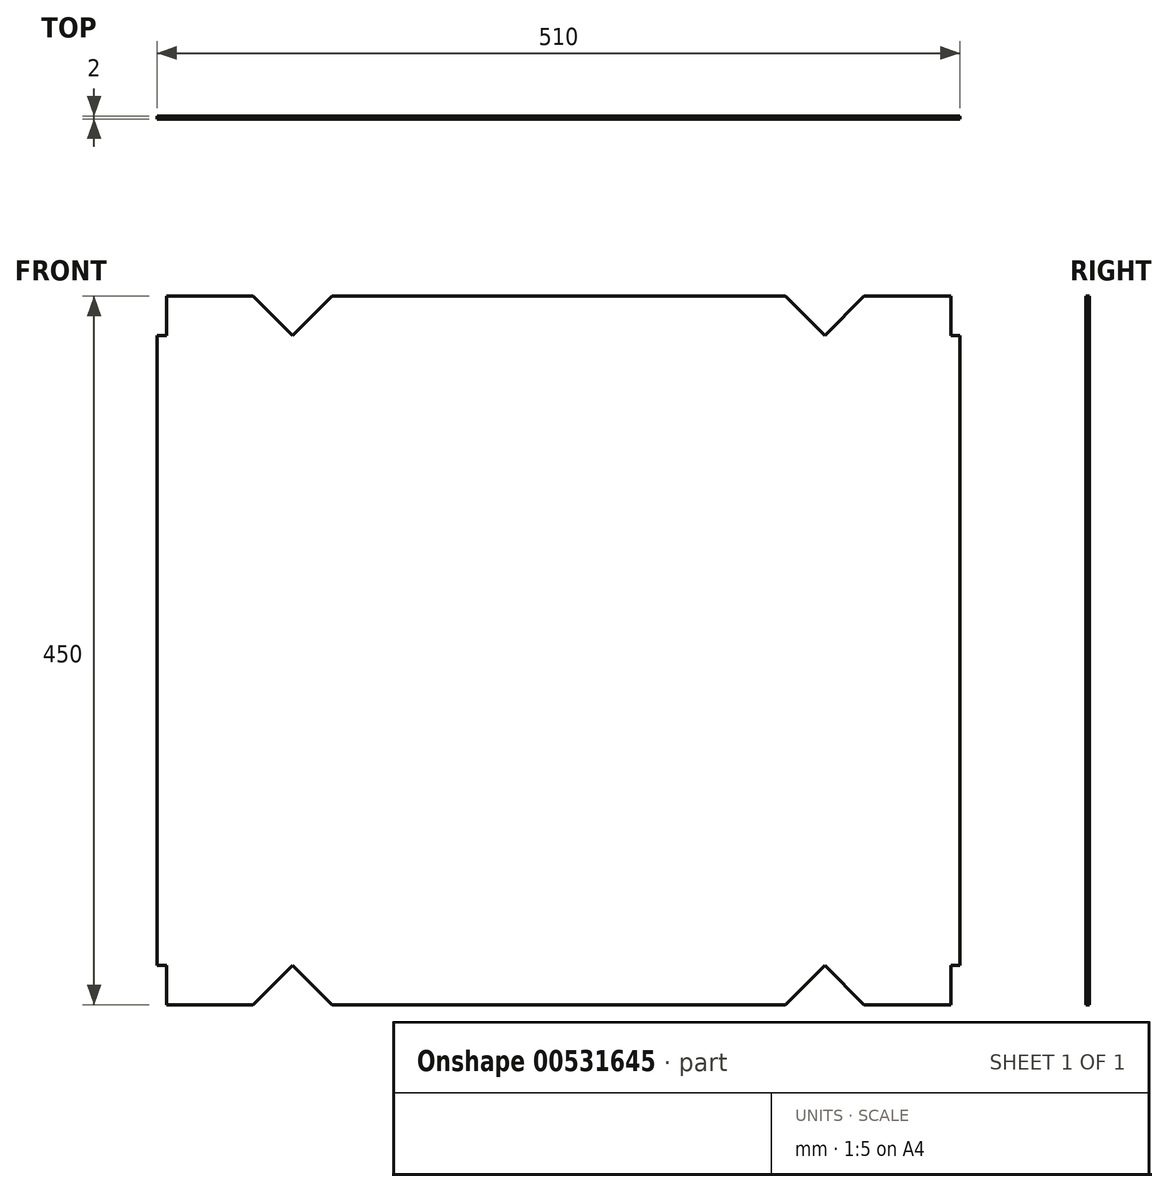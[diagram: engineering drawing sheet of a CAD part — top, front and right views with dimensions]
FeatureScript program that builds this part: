
annotation { "Feature Type Name" : "Feature", "Feature Type Description" : "" }
export const myFeature = defineFeature(function(context is Context, id is Id, definition is map)
    precondition{}
    {
        {
            var Q0;
            Q0=qCreatedBy(makeId("Front.planeOp"),FACE);
            var sketch = newSketch(context, id + "F0", { "sketchPlane" : qUnion([Q0])});
            skLineSegment(sketch, "E0.bottom", {"start": v(-246.48, 251.43) * mm, "end": v(-191.48, 251.43) * mm});
            skLineSegment(sketch, "E0.top", {"start": v(-246.48, -198.57) * mm, "end": v(-191.48, -198.57) * mm});
            skLineSegment(sketch, "E0.left", {"start": v(-252.48, 226.43) * mm, "end": v(-252.48, -173.57) * mm});
            skLineSegment(sketch, "E0.right", {"start": v(257.52, 226.43) * mm, "end": v(257.52, -173.57) * mm});
            skLineSegment(sketch, "E1.top", {"start": v(-252.48, 226.43) * mm, "end": v(-246.48, 226.43) * mm});
            skLineSegment(sketch, "E1.right", {"start": v(-246.48, 251.43) * mm, "end": v(-246.48, 226.43) * mm});
            skLineSegment(sketch, "E2.MirrorCS", {"start": v(251.52, 251.43) * mm, "end": v(251.52, 226.43) * mm});
            skLineSegment(sketch, "E3.MirrorCS", {"start": v(257.52, 226.43) * mm, "end": v(251.52, 226.43) * mm});
            skPoint(sketch, "E4.orphan", {"position": v(257.52, 251.43) * mm});
            skPoint(sketch, "E5.orphan", {"position": v(-252.48, 251.43) * mm});
            skLineSegment(sketch, "E6", {"start": v(-166.48, 226.43) * mm, "end": v(-141.48, 251.43) * mm});
            skLineSegment(sketch, "E7", {"start": v(-141.48, 251.43) * mm, "end": v(-166.48, 226.43) * mm});
            skLineSegment(sketch, "E8", {"start": v(-166.48, 226.43) * mm, "end": v(-191.48, 251.43) * mm});
            skLineSegment(sketch, "E9", {"start": v(-191.48, 251.43) * mm, "end": v(-166.48, 226.43) * mm});
            skLineSegment(sketch, "E10.MirrorCS", {"start": v(196.52, 251.43) * mm, "end": v(171.52, 226.43) * mm});
            skLineSegment(sketch, "E11.MirrorCS", {"start": v(171.52, 226.43) * mm, "end": v(146.52, 251.43) * mm});
            skLineSegment(sketch, "E12.trimOffspring", {"start": v(-141.48, 251.43) * mm, "end": v(146.52, 251.43) * mm});
            skLineSegment(sketch, "E13.trimOffspring", {"start": v(196.52, 251.43) * mm, "end": v(251.52, 251.43) * mm});
            skLineSegment(sketch, "E14", {"start": v(257.52, 226.43) * mm, "end": v(257.52, 26.43) * mm});
            skLineSegment(sketch, "E15.MirrorCS", {"start": v(171.52, -173.57) * mm, "end": v(146.52, -198.57) * mm});
            skLineSegment(sketch, "E16.MirrorCS", {"start": v(196.52, -198.57) * mm, "end": v(171.52, -173.57) * mm});
            skLineSegment(sketch, "E17.MirrorCS", {"start": v(251.52, -198.57) * mm, "end": v(251.52, -173.57) * mm});
            skLineSegment(sketch, "E18.MirrorCS", {"start": v(257.52, -173.57) * mm, "end": v(251.52, -173.57) * mm});
            skPoint(sketch, "E19.endSnap0", {"position": v(-252.48, 13.93) * mm});
            skLineSegment(sketch, "E20.MirrorCS", {"start": v(-191.48, -198.57) * mm, "end": v(-166.48, -173.57) * mm});
            skLineSegment(sketch, "E21.MirrorCS", {"start": v(-141.48, -198.57) * mm, "end": v(-166.48, -173.57) * mm});
            skLineSegment(sketch, "E22.MirrorCS", {"start": v(-246.48, -198.57) * mm, "end": v(-246.48, -173.57) * mm});
            skLineSegment(sketch, "E23.MirrorCS", {"start": v(-252.48, -173.57) * mm, "end": v(-246.48, -173.57) * mm});
            skPoint(sketch, "E19.end.orphan", {"position": v(-252.48, 26.43) * mm});
            skPoint(sketch, "E24.orphan", {"position": v(-252.48, -198.57) * mm});
            skLineSegment(sketch, "E25.trimOffspring", {"start": v(-141.48, -198.57) * mm, "end": v(146.52, -198.57) * mm});
            skLineSegment(sketch, "E26.trimOffspring", {"start": v(196.52, -198.57) * mm, "end": v(251.52, -198.57) * mm});
            skPoint(sketch, "E27.end.orphan", {"position": v(2.52, 251.43) * mm});
            skSolve(sketch);
        }
        {
            var Q0;
            Q0 = qSketchRegion(id + "F0", true);
            extrude(context, id + "F1", {"entities" : qUnion([Q0]), "depth" : 2 * mm, "offsetDistance" : 25 * mm});
        }
    });
